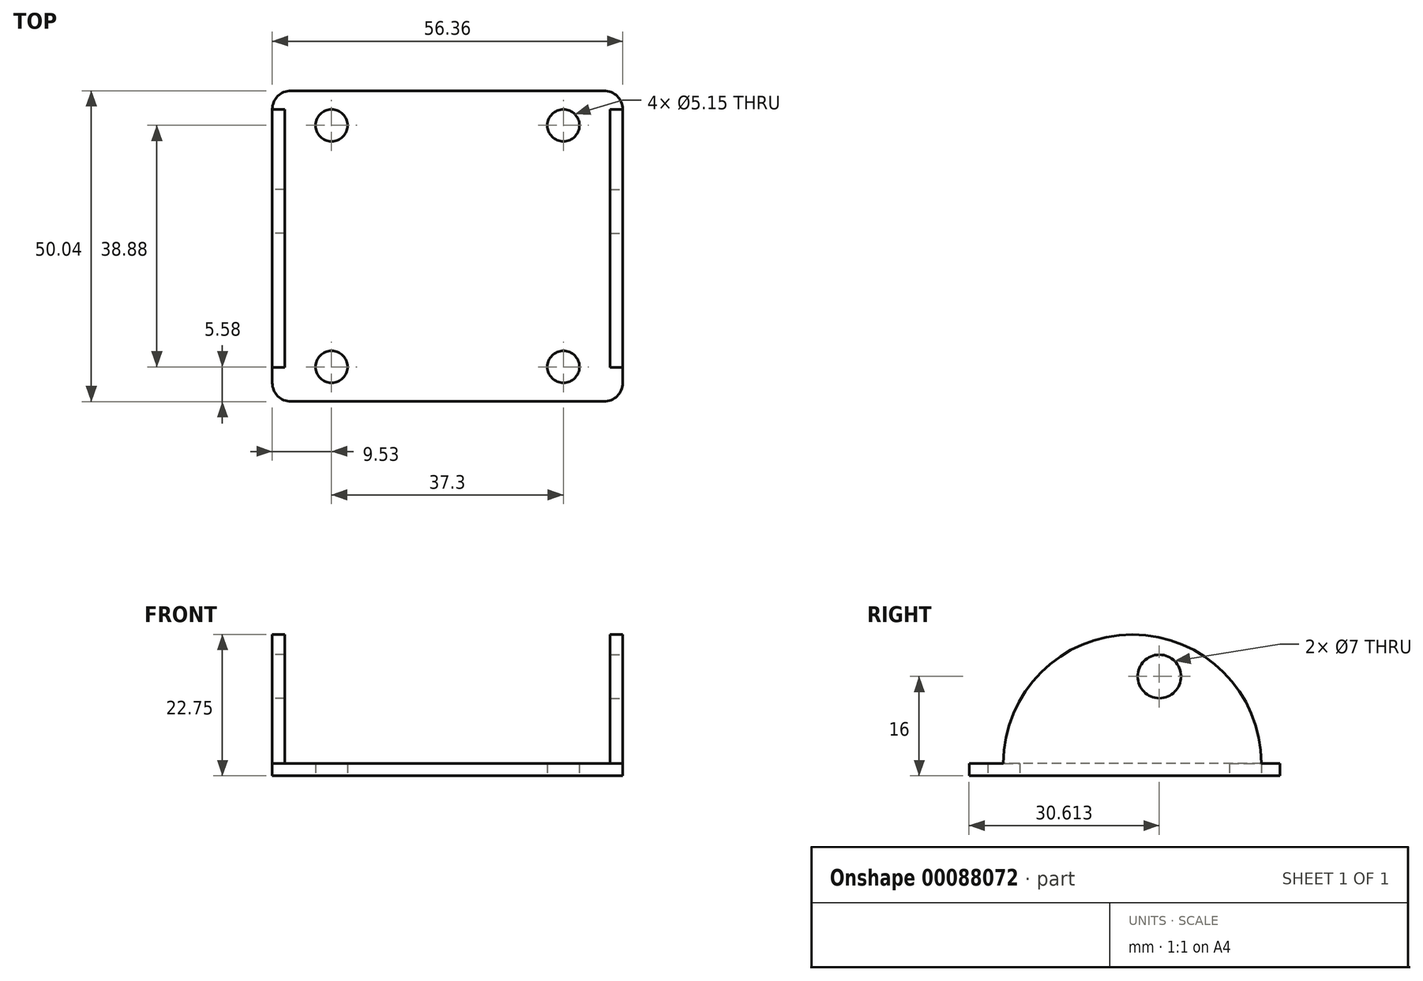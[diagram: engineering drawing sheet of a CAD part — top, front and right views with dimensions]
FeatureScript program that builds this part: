
annotation { "Feature Type Name" : "Feature", "Feature Type Description" : "" }
export const myFeature = defineFeature(function(context is Context, id is Id, definition is map)
    precondition{}
    {
        {
            var Q0;
            Q0=qCreatedBy(makeId("Top.planeOp"),FACE);
            var sketch = newSketch(context, id + "F0", { "sketchPlane" : qUnion([Q0])});
            skCircle(sketch, "E0", {"center": v(-18.65, 19.44) * mm, "radius": 2.58 * mm});
            skCircle(sketch, "E1.MirrorC", {"center": v(18.65, 19.44) * mm, "radius": 2.58 * mm});
            skCircle(sketch, "E2.MirrorC", {"center": v(-18.65, -19.44) * mm, "radius": 2.58 * mm});
            skCircle(sketch, "E3.MirrorC", {"center": v(18.65, -19.44) * mm, "radius": 2.58 * mm});
            skLineSegment(sketch, "E4", {"start": v(18.1, 25.02) * mm, "end": v(0, 25.02) * mm});
            skLineSegment(sketch, "E5.MirrorCS", {"start": v(-18.1, 25.02) * mm, "end": v(0, 25.02) * mm});
            skLineSegment(sketch, "E6.MirrorCS", {"start": v(18.1, -25.02) * mm, "end": v(0, -25.02) * mm});
            skLineSegment(sketch, "E7.MirrorCS", {"start": v(-18.1, -25.02) * mm, "end": v(0, -25.02) * mm});
            skLineSegment(sketch, "E8", {"start": v(28.17, 18.3) * mm, "end": v(28.18, -18.3) * mm});
            skLineSegment(sketch, "E9.MirrorCS", {"start": v(-28.17, 18.3) * mm, "end": v(-28.18, -18.3) * mm});
            skLineSegment(sketch, "E10", {"start": v(18.1, 25.02) * mm, "end": v(25.18, 25.02) * mm});
            skLineSegment(sketch, "E11", {"start": v(28.17, 22.02) * mm, "end": v(28.17, 18.3) * mm});
            skPoint(sketch, "E12.visualSharp", {"position": v(28.17, 25.02) * mm});
            skArc(sketch, "E12.filletArc", {"start": v(28.18, 22.02) * mm, "mid": v(27.3, 24.14) * mm, "end": v(25.18, 25.02) * mm});
            skLineSegment(sketch, "E13.MirrorCS", {"start": v(-18.1, 25.02) * mm, "end": v(-25.18, 25.02) * mm});
            skArc(sketch, "E14.MirrorCS", {"start": v(-28.18, 22.02) * mm, "mid": v(-27.3, 24.14) * mm, "end": v(-25.18, 25.02) * mm});
            skLineSegment(sketch, "E15.MirrorCS", {"start": v(-28.17, 22.02) * mm, "end": v(-28.17, 18.3) * mm});
            skLineSegment(sketch, "E16.MirrorCS", {"start": v(18.1, -25.02) * mm, "end": v(25.18, -25.02) * mm});
            skArc(sketch, "E17.MirrorCS", {"start": v(28.18, -22.02) * mm, "mid": v(27.3, -24.14) * mm, "end": v(25.18, -25.02) * mm});
            skLineSegment(sketch, "E18.MirrorCS", {"start": v(28.17, -22.02) * mm, "end": v(28.17, -18.3) * mm});
            skLineSegment(sketch, "E19.MirrorCS", {"start": v(-18.1, -25.02) * mm, "end": v(-25.18, -25.02) * mm});
            skArc(sketch, "E20.MirrorCS", {"start": v(-28.18, -22.02) * mm, "mid": v(-27.3, -24.14) * mm, "end": v(-25.18, -25.02) * mm});
            skLineSegment(sketch, "E21.MirrorCS", {"start": v(-28.17, -22.02) * mm, "end": v(-28.17, -18.3) * mm});
            skSolve(sketch);
        }
        {
            var Q0;
            Q0=makeQuery(id+"F0.imprint","IMPRINT",FACE,{"disambiguationData":[TD([[makeQuery(id+"F0.imprint","IMPRINT",EDGE,{"derivedFrom":sQuery(id+"F0.wireOp",EDGE,"E0")}),-1.0]])]});
            extrude(context, id + "F1", {"entities" : qUnion([Q0]), "depth" : 2 * mm});
        }
        {
            var Q0;
            Q0=makeQuery(id+"F1.opExtrude","SWEPT_FACE",FACE,{"disambiguationData":[OSD([sQuery(id+"F0.wireOp",EDGE,"E9.MirrorCS")])]});
            var sketch = newSketch(context, id + "F2", { "sketchPlane" : qUnion([Q0])});
            skArc(sketch, "E22", {"start": v(19.5, 2) * mm, "mid": v(-1.26, 22.75) * mm, "end": v(-22.02, 2) * mm});
            skCircle(sketch, "E23", {"center": v(-5.6, 16) * mm, "radius": 3.5 * mm});
            skLineSegment(sketch, "E24", {"start": v(-22.02, 2) * mm, "end": v(19.5, 2) * mm});
            skSolve(sketch);
        }
        {
            var Q0;
            Q0 = qSketchRegion(id + "F2", true);
            var Q1;
            {var subQ0=sQuery(id+"F2.wireOp",EDGE,"E22");Q1=makeQuery(id+"F2.imprint","IMPRINT",FACE,{"disambiguationData":[TD([[makeQuery(id+"F2.imprint","IMPRINT",EDGE,{"derivedFrom":subQ0}),1.0]])]});}
            extrude(context, id + "F3", {"entities" : qUnion([Q0, Q1]), "operationType" : NewBodyOperationType.ADD, "oppositeDirection" : true, "depth" : 2 * mm});
        }
        {
            var Q0;
            Q0=makeQuery(id+"F1.opExtrude","SWEPT_FACE",FACE,{"disambiguationData":[OSD([sQuery(id+"F0.wireOp",EDGE,"E8"),sQuery(id+"F0.wireOp",EDGE,"E11"),sQuery(id+"F0.wireOp",EDGE,"E18.MirrorCS")])]});
            var sketch = newSketch(context, id + "F4", { "sketchPlane" : qUnion([Q0])});
            skArc(sketch, "E25", {"start": v(22.02, 2) * mm, "mid": v(1.26, 22.75) * mm, "end": v(-19.5, 2) * mm});
            skCircle(sketch, "E26", {"center": v(5.6, 16) * mm, "radius": 3.5 * mm});
            skLineSegment(sketch, "E27", {"start": v(-19.5, 2) * mm, "end": v(22.02, 2) * mm});
            skSolve(sketch);
        }
        {
            var Q0;
            Q0 = qSketchRegion(id + "F4", true);
            extrude(context, id + "F5", {"entities" : qUnion([Q0]), "operationType" : NewBodyOperationType.ADD, "oppositeDirection" : true, "depth" : 2 * mm});
        }
    });
